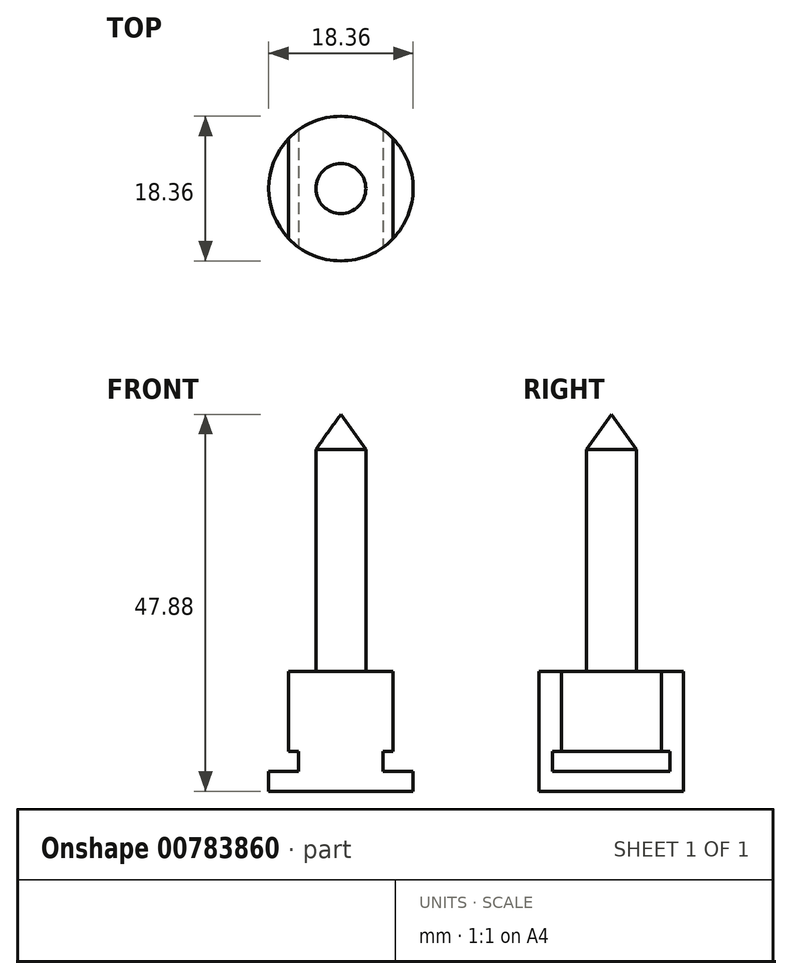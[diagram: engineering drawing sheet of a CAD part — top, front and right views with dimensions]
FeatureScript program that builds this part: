
annotation { "Feature Type Name" : "Feature", "Feature Type Description" : "" }
export const myFeature = defineFeature(function(context is Context, id is Id, definition is map)
    precondition{}
    {
        {
            var Q0;
            Q0=qCreatedBy(makeId("Top.planeOp"),FACE);
            var sketch = newSketch(context, id + "F0", { "sketchPlane" : qUnion([Q0])});
            skCircle(sketch, "E0", {"center": v(0, 0) * mm, "radius": 9.18 * mm});
            skSolve(sketch);
        }
        {
            var Q0;
            Q0 = qSketchRegion(id + "F0", true);
            extrude(context, id + "F1", {"entities" : qUnion([Q0]), "oppositeDirection" : true, "depth" : 15.24 * mm, "offsetDistance" : 25.4 * mm});
        }
        {
            var Q0;
            Q0=qCreatedBy(makeId("Front.planeOp"),FACE);
            var sketch = newSketch(context, id + "F2", { "sketchPlane" : qUnion([Q0])});
            skLineSegment(sketch, "E1", {"start": v(-9.18, -12.7) * mm, "end": v(-9.18, 0) * mm});
            skLineSegment(sketch, "E2.0", {"start": v(-6.64, -15.24) * mm, "end": v(6.64, -15.24) * mm});
            skLineSegment(sketch, "E3", {"start": v(9.18, 0) * mm, "end": v(9.18, -12.7) * mm});
            skLineSegment(sketch, "E4", {"start": v(-9.18, -12.7) * mm, "end": v(-9.18, 0) * mm, "construction": true});
            skLineSegment(sketch, "E5", {"start": v(9.18, 0) * mm, "end": v(9.18, -12.7) * mm, "construction": true});
            skLineSegment(sketch, "E6.bottom", {"start": v(6.64, -15.24) * mm, "end": v(-6.64, -15.24) * mm, "construction": true});
            skLineSegment(sketch, "E6.top", {"start": v(6.64, -12.7) * mm, "end": v(-6.64, -12.7) * mm, "construction": true});
            skPoint(sketch, "E6.middle", {"position": v(0, -13.97) * mm});
            skLineSegment(sketch, "E7.bottom", {"start": v(5.37, -12.7) * mm, "end": v(-5.37, -12.7) * mm, "construction": true});
            skLineSegment(sketch, "E7.top", {"start": v(5.37, -10.16) * mm, "end": v(-5.37, -10.16) * mm, "construction": true});
            skLineSegment(sketch, "E7.left", {"start": v(5.37, -12.7) * mm, "end": v(5.37, -10.16) * mm, "construction": true});
            skLineSegment(sketch, "E7.right", {"start": v(-5.37, -12.7) * mm, "end": v(-5.37, -10.16) * mm, "construction": true});
            skPoint(sketch, "E7.middle", {"position": v(0, -11.43) * mm});
            skLineSegment(sketch, "E8", {"start": v(0, 0) * mm, "end": v(0, -10.16) * mm, "construction": true});
            skLineSegment(sketch, "E9.bottom", {"start": v(6.64, -10.16) * mm, "end": v(-6.64, -10.16) * mm, "construction": true});
            skLineSegment(sketch, "E9.top", {"start": v(6.64, 0) * mm, "end": v(-6.64, 0) * mm, "construction": true});
            skLineSegment(sketch, "E9.left", {"start": v(6.64, -10.16) * mm, "end": v(6.64, 0) * mm, "construction": true});
            skLineSegment(sketch, "E9.right", {"start": v(-6.64, -10.16) * mm, "end": v(-6.64, 0) * mm, "construction": true});
            skPoint(sketch, "E9.middle", {"position": v(0, -5.08) * mm});
            skLineSegment(sketch, "E10.bottom", {"start": v(-9.18, 0) * mm, "end": v(-6.64, 0) * mm});
            skLineSegment(sketch, "E10.left", {"start": v(-9.18, 0) * mm, "end": v(-9.18, -12.7) * mm});
            skLineSegment(sketch, "E10.right", {"start": v(-6.64, 0) * mm, "end": v(-6.64, -10.16) * mm});
            skLineSegment(sketch, "E11.bottom", {"start": v(-6.64, -10.16) * mm, "end": v(-5.37, -10.16) * mm});
            skLineSegment(sketch, "E11.top", {"start": v(-6.64, -12.7) * mm, "end": v(-5.37, -12.7) * mm});
            skLineSegment(sketch, "E11.right", {"start": v(-5.37, -10.16) * mm, "end": v(-5.37, -12.7) * mm});
            skLineSegment(sketch, "E12.bottom", {"start": v(6.64, 0) * mm, "end": v(9.18, 0) * mm});
            skLineSegment(sketch, "E12.left", {"start": v(6.64, 0) * mm, "end": v(6.64, -10.16) * mm});
            skLineSegment(sketch, "E13.bottom", {"start": v(5.37, -10.16) * mm, "end": v(6.64, -10.16) * mm});
            skLineSegment(sketch, "E13.top", {"start": v(5.37, -12.7) * mm, "end": v(6.64, -12.7) * mm});
            skLineSegment(sketch, "E13.left", {"start": v(5.37, -10.16) * mm, "end": v(5.37, -12.7) * mm});
            skLineSegment(sketch, "E14", {"start": v(-6.64, -12.7) * mm, "end": v(-9.18, -12.7) * mm});
            skLineSegment(sketch, "E15", {"start": v(6.64, -12.7) * mm, "end": v(9.18, -12.7) * mm});
            skPoint(sketch, "E16.orphan", {"position": v(-9.18, -15.24) * mm});
            skPoint(sketch, "E17.orphan", {"position": v(9.18, -15.24) * mm});
            skSolve(sketch);
        }
        {
            var Q0;
            Q0 = qSketchRegion(id + "F2", true);
            extrude(context, id + "F3", {"entities" : qUnion([Q0]), "operationType" : NewBodyOperationType.REMOVE, "endBound" : BoundingType.THROUGH_ALL, "oppositeDirection" : true, "depth" : 25.4 * mm, "offsetDistance" : 25.4 * mm, "hasSecondDirection" : true, "secondDirectionBound" : BoundingType.THROUGH_ALL, "secondDirectionOppositeDirection" : false, "secondDirectionDepth" : 25.4 * mm});
        }
        {
            var Q0;
            Q0=qCreatedBy(makeId("Front.planeOp"),FACE);
            var sketch = newSketch(context, id + "F4", { "sketchPlane" : qUnion([Q0])});
            skLineSegment(sketch, "E18.0", {"start": v(-6.64, 0) * mm, "end": v(6.64, 0) * mm});
            skLineSegment(sketch, "E19", {"start": v(0, 0) * mm, "end": v(0, 32.64) * mm});
            skLineSegment(sketch, "E20", {"start": v(0, 0) * mm, "end": v(3.18, 0) * mm});
            skLineSegment(sketch, "E21", {"start": v(3.18, 0) * mm, "end": v(3.18, 28.19) * mm});
            skLineSegment(sketch, "E22", {"start": v(3.17, 28.19) * mm, "end": v(0, 32.64) * mm});
            skLineSegment(sketch, "E23", {"start": v(0, 0) * mm, "end": v(0, 30.6) * mm, "construction": true});
            skSolve(sketch);
        }
        {
            var Q0;
            Q0 = qSketchRegion(id + "F4", true);
            var Q1;
            Q1=sQuery(id+"F4.wireOp",EDGE,"E23");
            revolve(context, id + "F5", {"operationType" : NewBodyOperationType.ADD, "surfaceOperationType" : NewSurfaceOperationType.NEW, "entities" : qUnion([Q0]), "axis" : qUnion([Q1]), "revolveType" : RevolveType.FULL});
        }
    });
